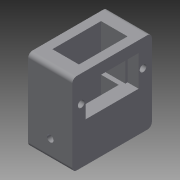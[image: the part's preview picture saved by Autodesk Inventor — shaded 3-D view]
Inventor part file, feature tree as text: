
AUTODESK INVENTOR PART (.ipt)
format: ipt  version: 2015 SP1 (Build 190203100, 203)  size: 205,824 bytes
history: native  units: mm
features: sketch x11, extrude x9, projected_geometry x7, reference x2, other x1, fillet x1, plane x1
ambient origin geometry x8: Origin, YZ Plane, XZ Plane, XY Plane, X Axis, Y Axis, Z Axis, Center Point
bodies: Body1 (feature_tree)
feature tree (32):
  other  "Sólido1"
  sketch  "Boceto1"  dims[d0=10.0mm d1=20.0mm]
  extrude  "Extrusión1"  Depth=20.0mm
  extrude  "Extrusión2"  Depth=36.0mm
  extrude  "Extrusión3"  Depth=22.0mm TaperAngle=0.0deg
  extrude  "Extrusión4"  Depth=14.0mm
  fillet  "Empalme1"  Radius=14.0mm
  sketch  "Boceto7"  dims[d14=2.0mm d15=3.0mm]
  sketch  "Boceto8"  dims[d16=2.0mm d17=3.0mm]
  plane  "Plano de trabajo1"
  extrude  "Extrusión6"  Depth=5.0mm TaperAngle=0.0deg
  extrude  "Extrusión7"  Depth=3.0mm
  extrude  "Extrusión8"  Depth=3.0mm
  extrude  "Extrusión9"  Depth=2.0mm
  extrude  "Extrusión10"  Depth=20.0mm TaperAngle=0.0deg
  sketch  "Boceto2"  dims[d2=20.0mm d3=36.0mm]
  reference  "Referencia1"
  sketch  "Boceto3"  dims[d4=15.0mm d5=0.0mm d6=22.0mm d7=0.0mm]
  reference  "Referencia2"
  projected_geometry  "Contorno proyectado1"
  sketch  "Boceto4"  dims[d8=5.0mm d9=12.0mm d10=14.0mm]
  projected_geometry  "Contorno proyectado2"
  sketch  "Boceto5"  dims[d11=24.0mm d12=5.0mm d13=0.0mm]
  projected_geometry  "Contorno proyectado4"
  sketch  "Boceto9"  dims[d18=15.0mm d19=0.0mm d20=2.0mm]
  projected_geometry  "Contorno proyectado5"
  sketch  "Boceto10"  dims[d28=20.0mm d29=0.0mm d30=100.0mm d31=0.0mm]
  projected_geometry  "Contorno proyectado6"
  sketch  "Boceto11"  dims[d32=8.0mm]
  projected_geometry  "Contorno proyectado7"
  sketch  "Boceto12"  dims[d33=18.0mm d34=20.0mm d35=0.0mm d36=20.0mm d37=0.0mm d38=50.0mm d39=0.0mm]
  projected_geometry  "Contorno proyectado8"
